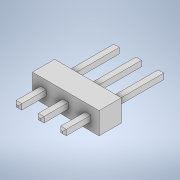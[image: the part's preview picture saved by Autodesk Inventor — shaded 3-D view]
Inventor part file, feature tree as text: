
AUTODESK INVENTOR PART (.ipt)
format: ipt  version: 2022 (Build 260153000, 153)  size: 171,008 bytes
history: native  units: mm
features: extrude x3, sketch x3, projected_geometry x3, chamfer x1
ambient origin geometry x8: Origin, YZ Plane, XZ Plane, XY Plane, X Axis, Y Axis, Z Axis, Center Point
bodies: Solid1 (feature_tree)
feature tree (10):
  extrude  "Extrusion1"  Depth=2.5mm
  extrude  "Extrusion2"  Depth=0.64mm
  extrude  "Extrusion3"  Depth=0.64mm
  chamfer  "Chamfer1"  Distance=0.64mm
  sketch  "Sketch1"  dims[d0=7.62mm d1=2.5mm]
  sketch  "Sketch2"  dims[d2=2.54mm d3=0.0mm d4=0.64mm]
  sketch  "Sketch3"  dims[d5=0.64mm d6=0.64mm d7=0.64mm d8=2.54mm d9=2.54mm d10=0.93mm d11=0.95mm d12=3.0mm d13=0.0mm d14=6.0mm d15=0.0mm d16=0.2mm d17=2.0mm d18=45.0deg]
  projected_geometry  "Projected Loop1"
  projected_geometry  "Projected Loop2"
  projected_geometry  "Projected Loop3"
